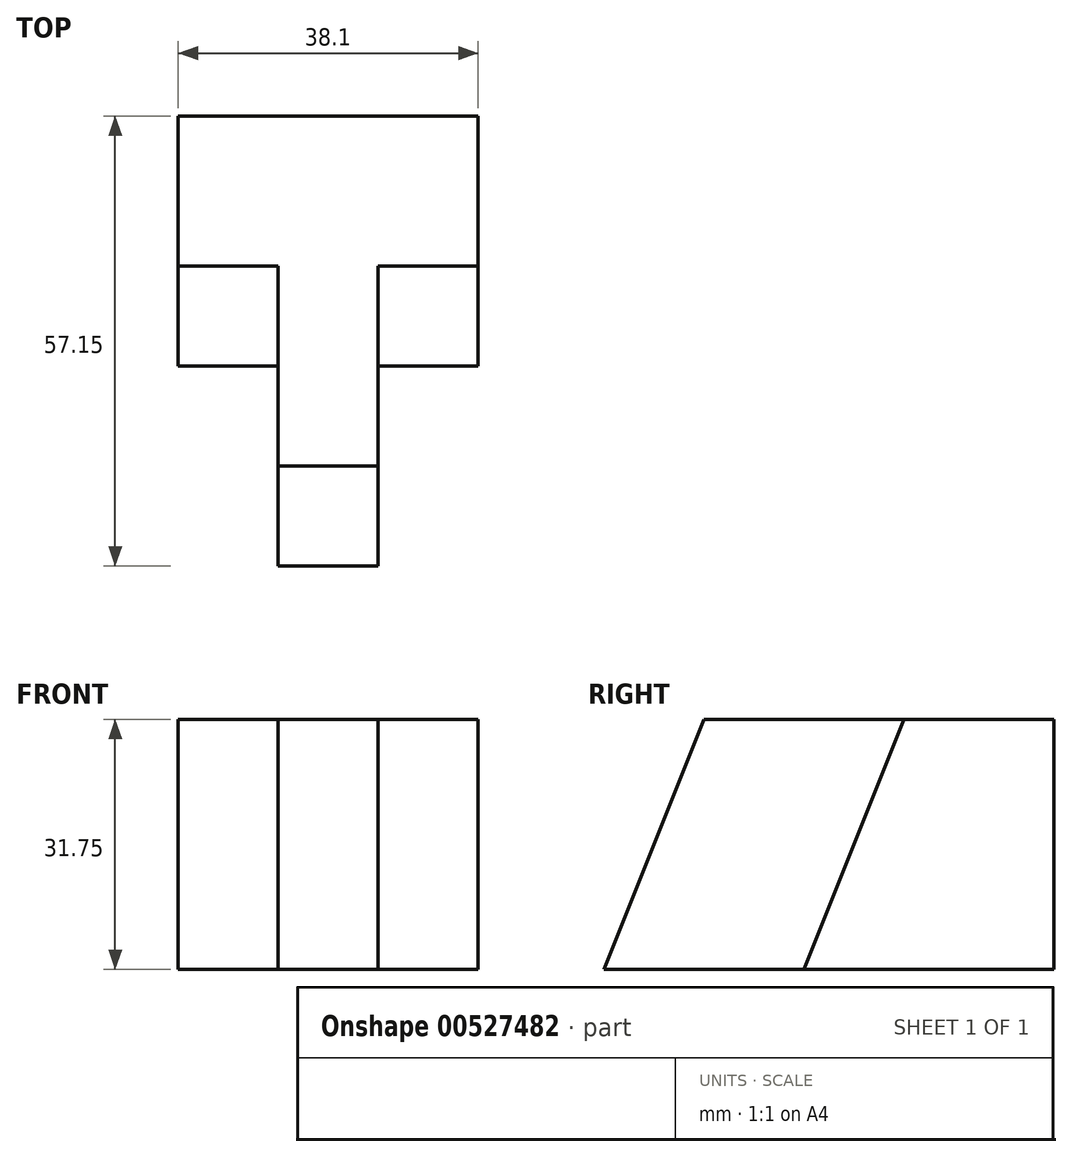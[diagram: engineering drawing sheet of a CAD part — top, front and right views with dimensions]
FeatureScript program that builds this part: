
annotation { "Feature Type Name" : "Feature", "Feature Type Description" : "" }
export const myFeature = defineFeature(function(context is Context, id is Id, definition is map)
    precondition{}
    {
        {
            var Q0;
            Q0=qCreatedBy(makeId("Right.planeOp"),FACE);
            var sketch = newSketch(context, id + "F0", { "sketchPlane" : qUnion([Q0])});
            skLineSegment(sketch, "E0", {"start": v(0, 0) * mm, "end": v(57.15, 0) * mm});
            skLineSegment(sketch, "E1", {"start": v(0, 0) * mm, "end": v(0, 31.75) * mm});
            skLineSegment(sketch, "E2", {"start": v(0, 31.75) * mm, "end": v(57.15, 31.75) * mm});
            skLineSegment(sketch, "E3", {"start": v(57.15, 31.75) * mm, "end": v(57.15, 0) * mm});
            skSolve(sketch);
        }
        {
            var Q0;
            Q0 = qSketchRegion(id + "F0", true);
            extrude(context, id + "F1", {"entities" : qUnion([Q0]), "oppositeDirection" : true, "depth" : 38.1 * mm, "offsetDistance" : 25.4 * mm});
        }
        {
            var Q0;
            Q0=makeQuery(id+"F1.opExtrude","CAP_FACE",FACE,{"disambiguationData":[OSD([sQuery(id+"F0.wireOp",EDGE,"E0"),sQuery(id+"F0.wireOp",EDGE,"E1"),sQuery(id+"F0.wireOp",EDGE,"E2"),sQuery(id+"F0.wireOp",EDGE,"E3")])],"isStart":false});
            var sketch = newSketch(context, id + "F2", { "sketchPlane" : qUnion([Q0])});
            skLineSegment(sketch, "E4", {"start": v(-38.1, 31.75) * mm, "end": v(-25.4, 0) * mm});
            skSolve(sketch);
        }
        {
            var Q0;
            {var subQ0=sQuery(id+"F2.wireOp",EDGE,"E4");Q0=makeQuery(id+"F2.imprint","IMPRINT",FACE,{"disambiguationData":[TD([[makeQuery(id+"F2.imprint","IMPRINT",EDGE,{"derivedFrom":subQ0}),1.0]])]});}
            extrude(context, id + "F3", {"entities" : qUnion([Q0]), "operationType" : NewBodyOperationType.REMOVE, "oppositeDirection" : true, "depth" : 12.7 * mm, "offsetDistance" : 25.4 * mm});
        }
        {
            var Q0;
            Q0=makeQuery(id+"F1.opExtrude","CAP_FACE",FACE,{"disambiguationData":[OSD([sQuery(id+"F0.wireOp",EDGE,"E0"),sQuery(id+"F0.wireOp",EDGE,"E1"),sQuery(id+"F0.wireOp",EDGE,"E2"),sQuery(id+"F0.wireOp",EDGE,"E3")])],"isStart":true});
            var sketch = newSketch(context, id + "F4", { "sketchPlane" : qUnion([Q0])});
            skLineSegment(sketch, "E5", {"start": v(38.1, 31.75) * mm, "end": v(25.4, 0) * mm});
            skSolve(sketch);
        }
        {
            var Q0;
            {var subQ0=sQuery(id+"F4.wireOp",EDGE,"E5");Q0=makeQuery(id+"F4.imprint","IMPRINT",FACE,{"disambiguationData":[TD([[makeQuery(id+"F4.imprint","IMPRINT",EDGE,{"derivedFrom":subQ0}),-1.0]])]});}
            extrude(context, id + "F5", {"entities" : qUnion([Q0]), "operationType" : NewBodyOperationType.REMOVE, "oppositeDirection" : true, "depth" : 12.7 * mm, "offsetDistance" : 25.4 * mm});
        }
        {
            var Q0;
            Q0=makeQuery(id+"F5.boolean.opBoolean","COPY",FACE,{"derivedFrom":makeQuery(id+"F5.opExtrude","CAP_FACE",FACE,{"disambiguationData":[OSD([sQuery(id+"F0.wireOp",EDGE,"E0"),sQuery(id+"F0.wireOp",EDGE,"E1"),sQuery(id+"F0.wireOp",EDGE,"E2"),sQuery(id+"F4.wireOp",EDGE,"E5")])],"isStart":false})});
            var sketch = newSketch(context, id + "F6", { "sketchPlane" : qUnion([Q0])});
            skLineSegment(sketch, "E6", {"start": v(12.7, 31.75) * mm, "end": v(0, 0) * mm});
            skSolve(sketch);
        }
        {
            var Q0;
            {var subQ0=sQuery(id+"F6.wireOp",EDGE,"E6");Q0=makeQuery(id+"F6.imprint","IMPRINT",FACE,{"disambiguationData":[TD([[makeQuery(id+"F6.imprint","IMPRINT",EDGE,{"derivedFrom":subQ0}),-1.0]])]});}
            extrude(context, id + "F7", {"entities" : qUnion([Q0]), "operationType" : NewBodyOperationType.REMOVE, "oppositeDirection" : true, "depth" : 12.7 * mm, "offsetDistance" : 25.4 * mm});
        }
    });
